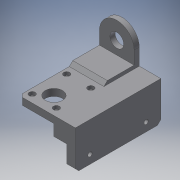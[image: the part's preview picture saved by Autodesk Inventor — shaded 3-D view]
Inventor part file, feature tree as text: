
AUTODESK INVENTOR PART (.ipt)
format: ipt  version: 2017 (Build 210142000, 142)  size: 239,616 bytes
history: native  units: mm
features: extrude x8, sketch x8, projected_geometry x4, other x2, chamfer x1, reference x1
ambient origin geometry x8: Origin, YZ Plane, XZ Plane, XY Plane, X Axis, Y Axis, Z Axis, Center Point
bodies: Solid1 (feature_tree)
feature tree (24):
  extrude  "Extrusion1"  Depth=40.0mm
  extrude  "Extrusion2"  Depth=20.0mm
  extrude  "Extrusion3"  Depth=40.12mm
  extrude  "Extrusion4"  Depth=8.0mm TaperAngle=0.0deg
  extrude  "Extrusion5"  Depth=4.0mm TaperAngle=0.0deg
  extrude  "Extrusion6"  Depth=35.0mm TaperAngle=0.0deg
  extrude  "Extrusion7"  Depth=16.0mm
  extrude  "Extrusion8"  TaperAngle=60.0deg  [1 undecoded]
  chamfer  "Chamfer1"  Distance=25.0mm
  sketch  "Sketch1"  dims[d0=28.0mm d1=40.0mm]
  sketch  "Sketch2"  dims[d2=20.0mm d3=4.5mm]
  projected_geometry  "Projected Loop1"
  sketch  "Sketch3"  dims[d4=58.1mm d5=40.12mm]
  sketch  "Sketch4"  dims[d6=37.9mm d7=8.0mm d8=0.0mm]
  reference  "Reference1"
  projected_geometry  "Projected Loop2"
  sketch  "Sketch5"  dims[d9=7.0mm d10=4.0mm d11=0.0mm]
  sketch  "Sketch6"  dims[d12=12.0mm d13=35.0mm d14=0.0mm]
  projected_geometry  "Projected Loop3"
  sketch  "Sketch7"  dims[d15=27.0mm d16=16.0mm]
  sketch  "Sketch8"  dims[d17=6.0mm d18=0.0mm d19=60.0deg d20=25.0mm d21=25.0mm d22=10.0mm d23=0.0mm d24=10.0mm d25=0.0mm d26=20.0mm d27=10.0mm d28=0.0mm d29=65.0mm d30=5.0mm d31=10.0mm d32=0.0mm d33=4.0mm d34=2.0mm d35=45.0deg]
  projected_geometry  "Projected Loop4"
  other  "circulation pump.iam"
  other  "motor:1"
note: 1 required parameter value undecoded (feature->parameter linkage not recoverable at this tier; creation-order binding heuristic only, values carry confidence <= 0.55)
